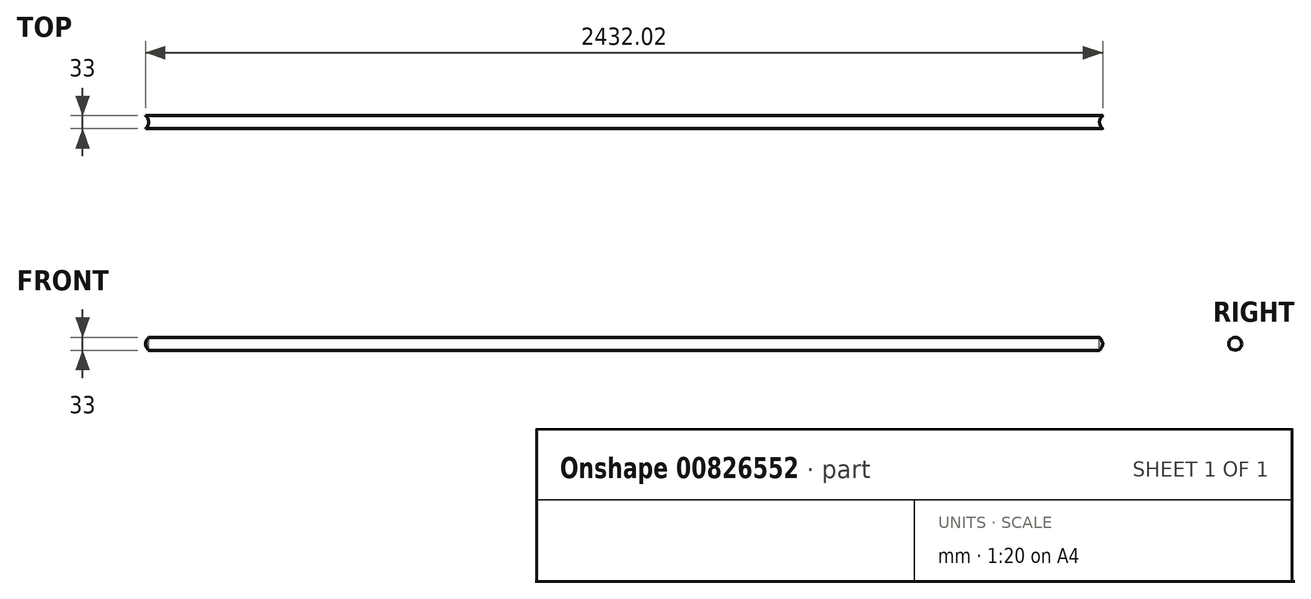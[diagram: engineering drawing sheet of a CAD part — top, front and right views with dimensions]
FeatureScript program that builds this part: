
annotation { "Feature Type Name" : "Feature", "Feature Type Description" : "" }
export const myFeature = defineFeature(function(context is Context, id is Id, definition is map)
    precondition{}
    {
        {
            var Q0;
            Q0=qCreatedBy(makeId("Right.planeOp"),FACE);
            var sketch = newSketch(context, id + "F0", { "sketchPlane" : qUnion([Q0])});
            skCircle(sketch, "E0", {"center": v(0, 0) * mm, "radius": 16.5 * mm});
            skSolve(sketch);
        }
        {
            var Q0;
            Q0=makeQuery(id+"F0.imprint","IMPRINT",FACE,{"disambiguationData":[TD([[makeQuery(id+"F0.imprint","IMPRINT",EDGE,{"derivedFrom":sQuery(id+"F0.wireOp",EDGE,"E0")}),1.0]])]});
            extrude(context, id + "F1", {"entities" : qUnion([Q0]), "depth" : (2500 - 42) * mm, "offsetDistance" : 25 * mm});
        }
        {
            var Q0;
            Q0=qCreatedBy(makeId("Top.planeOp"),FACE);
            var sketch = newSketch(context, id + "F2", { "sketchPlane" : qUnion([Q0])});
            skCircle(sketch, "E1", {"center": v(0, 0) * mm, "radius": 21 * mm});
            skLineSegment(sketch, "E2", {"start": v(0, 0) * mm, "end": v(2458, 0) * mm});
            skCircle(sketch, "E3", {"center": v(2458, 0) * mm, "radius": 21 * mm});
            skSolve(sketch);
        }
        {
            var Q0;
            Q0=makeQuery(id+"F2.imprint","IMPRINT",FACE,{"disambiguationData":[TD([[makeQuery(id+"F2.imprint","IMPRINT",EDGE,{"derivedFrom":sQuery(id+"F2.wireOp",EDGE,"E3")}),1.0]])]});
            var Q1;
            Q1=makeQuery(id+"F2.imprint","IMPRINT",FACE,{"disambiguationData":[TD([[makeQuery(id+"F2.imprint","IMPRINT",EDGE,{"derivedFrom":sQuery(id+"F2.wireOp",EDGE,"E1")}),1.0]])]});
            extrude(context, id + "F3", {"entities" : qUnion([Q0, Q1]), "operationType" : NewBodyOperationType.REMOVE, "endBound" : BoundingType.SYMMETRIC, "oppositeDirection" : true, "depth" : 200 * mm, "offsetDistance" : 25 * mm});
        }
    });
